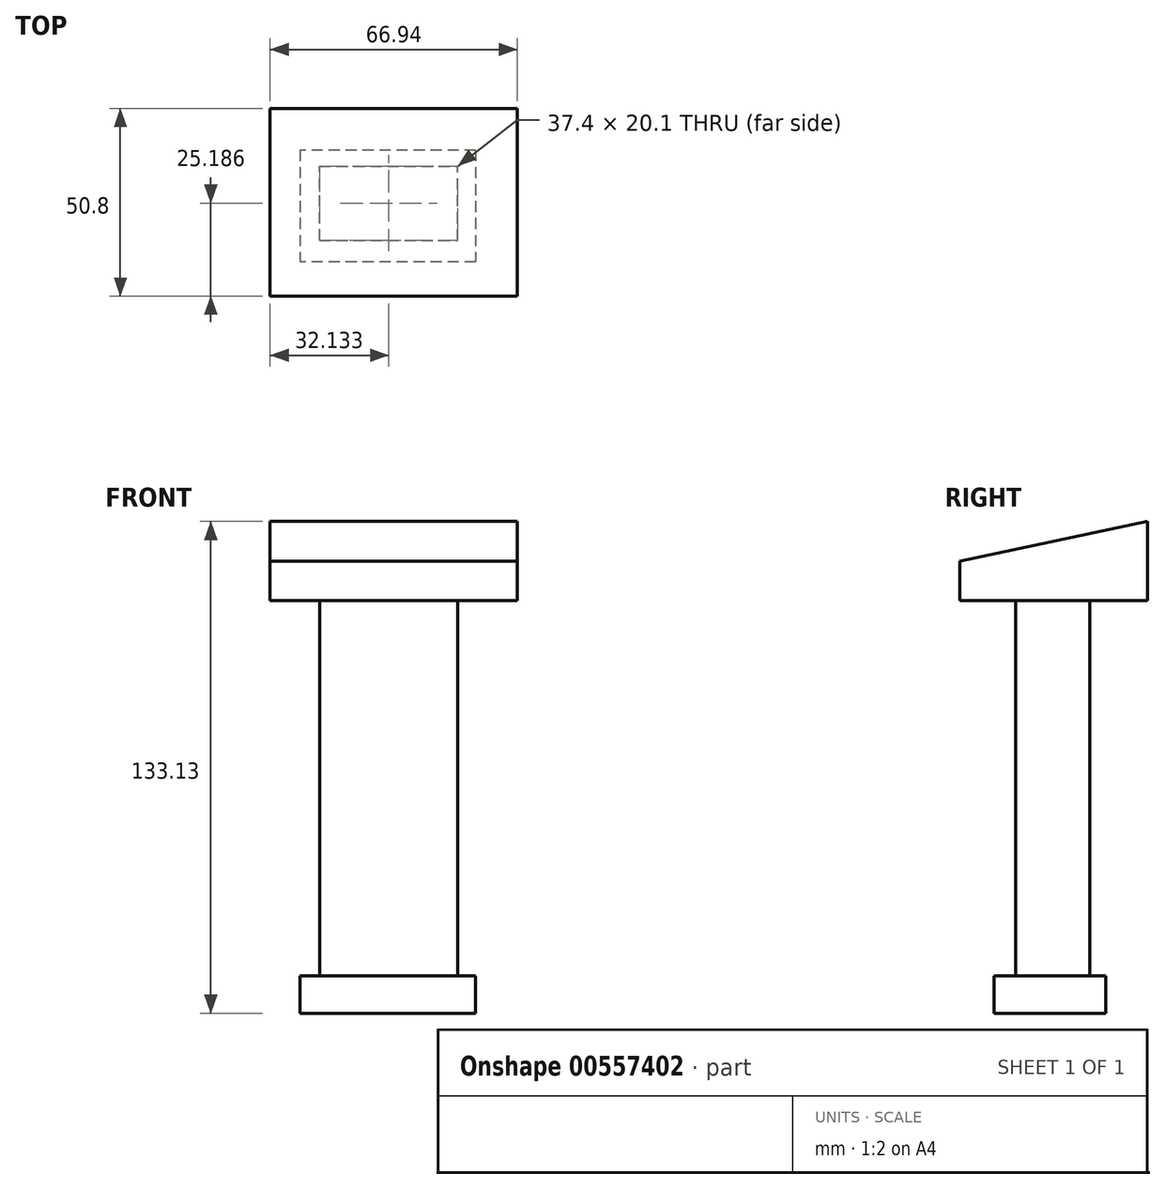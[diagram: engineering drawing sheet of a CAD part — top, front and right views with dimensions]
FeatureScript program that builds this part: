
annotation { "Feature Type Name" : "Feature", "Feature Type Description" : "" }
export const myFeature = defineFeature(function(context is Context, id is Id, definition is map)
    precondition{}
    {
        {
            var Q0;
            Q0=qCreatedBy(makeId("Front.planeOp"),FACE);
            var sketch = newSketch(context, id + "F0", { "sketchPlane" : qUnion([Q0])});
            skLineSegment(sketch, "E0.bottom", {"start": v(-35.44, 19.2) * mm, "end": v(31.5, 19.2) * mm});
            skLineSegment(sketch, "E0.top", {"start": v(-35.44, -2.16) * mm, "end": v(31.5, -2.16) * mm});
            skLineSegment(sketch, "E0.left", {"start": v(-35.44, 19.2) * mm, "end": v(-35.44, -2.16) * mm});
            skLineSegment(sketch, "E0.right", {"start": v(31.5, 19.2) * mm, "end": v(31.5, -2.16) * mm});
            skSolve(sketch);
        }
        {
            var Q0;
            Q0 = qSketchRegion(id + "F0", true);
            extrude(context, id + "F1", {"entities" : qUnion([Q0]), "oppositeDirection" : true, "depth" : 50.8 * mm, "offsetDistance" : 25.4 * mm});
        }
        {
            var Q0;
            Q0=makeQuery(id+"F1.opExtrude","SWEPT_FACE",FACE,{"disambiguationData":[OSD([sQuery(id+"F0.wireOp",EDGE,"E0.left")])]});
            var sketch = newSketch(context, id + "F2", { "sketchPlane" : qUnion([Q0])});
            skLineSegment(sketch, "E1", {"start": v(-50.8, 19.2) * mm, "end": v(0, 8.52) * mm});
            skSolve(sketch);
        }
        {
            var Q0;
            {var subQ0=sQuery(id+"F2.wireOp",EDGE,"E1");Q0=makeQuery(id+"F2.imprint","IMPRINT",FACE,{"disambiguationData":[TD([[makeQuery(id+"F2.imprint","IMPRINT",EDGE,{"derivedFrom":subQ0}),1.0]])]});}
            extrude(context, id + "F3", {"entities" : qUnion([Q0]), "operationType" : NewBodyOperationType.REMOVE, "oppositeDirection" : true, "depth" : 76.2 * mm, "offsetDistance" : 25.4 * mm});
        }
        {
            var Q0;
            Q0=makeQuery(id+"F1.opExtrude","SWEPT_FACE",FACE,{"disambiguationData":[OSD([sQuery(id+"F0.wireOp",EDGE,"E0.top")])]});
            var sketch = newSketch(context, id + "F4", { "sketchPlane" : qUnion([Q0])});
            skLineSegment(sketch, "E2.bottom", {"start": v(-22, -15.14) * mm, "end": v(15.4, -15.14) * mm});
            skLineSegment(sketch, "E2.top", {"start": v(-22, -35.23) * mm, "end": v(15.4, -35.23) * mm});
            skLineSegment(sketch, "E2.left", {"start": v(-22, -15.14) * mm, "end": v(-22, -35.23) * mm});
            skLineSegment(sketch, "E2.right", {"start": v(15.4, -15.14) * mm, "end": v(15.4, -35.23) * mm});
            skSolve(sketch);
        }
        {
            var Q0;
            Q0 = qSketchRegion(id + "F4", true);
            extrude(context, id + "F5", {"entities" : qUnion([Q0]), "operationType" : NewBodyOperationType.ADD, "depth" : 101.6 * mm, "offsetDistance" : 25.4 * mm});
        }
        {
            var Q0;
            Q0=makeQuery(id+"F5.opExtrude","CAP_FACE",FACE,{"disambiguationData":[OSD([sQuery(id+"F4.wireOp",EDGE,"E2.bottom"),sQuery(id+"F4.wireOp",EDGE,"E2.top"),sQuery(id+"F4.wireOp",EDGE,"E2.left"),sQuery(id+"F4.wireOp",EDGE,"E2.right")])],"isStart":false});
            var sketch = newSketch(context, id + "F6", { "sketchPlane" : qUnion([Q0])});
            skLineSegment(sketch, "E3.bottom", {"start": v(20.23, -39.56) * mm, "end": v(-27.35, -39.56) * mm});
            skLineSegment(sketch, "E3.top", {"start": v(20.23, -9.29) * mm, "end": v(-27.35, -9.29) * mm});
            skLineSegment(sketch, "E3.left", {"start": v(20.23, -39.56) * mm, "end": v(20.23, -9.29) * mm});
            skLineSegment(sketch, "E3.right", {"start": v(-27.35, -39.56) * mm, "end": v(-27.35, -9.29) * mm});
            skSolve(sketch);
        }
        {
            var Q0;
            Q0 = qSketchRegion(id + "F6", true);
            extrude(context, id + "F7", {"entities" : qUnion([Q0]), "operationType" : NewBodyOperationType.ADD, "depth" : 10.16 * mm, "offsetDistance" : 25.4 * mm});
        }
    });
